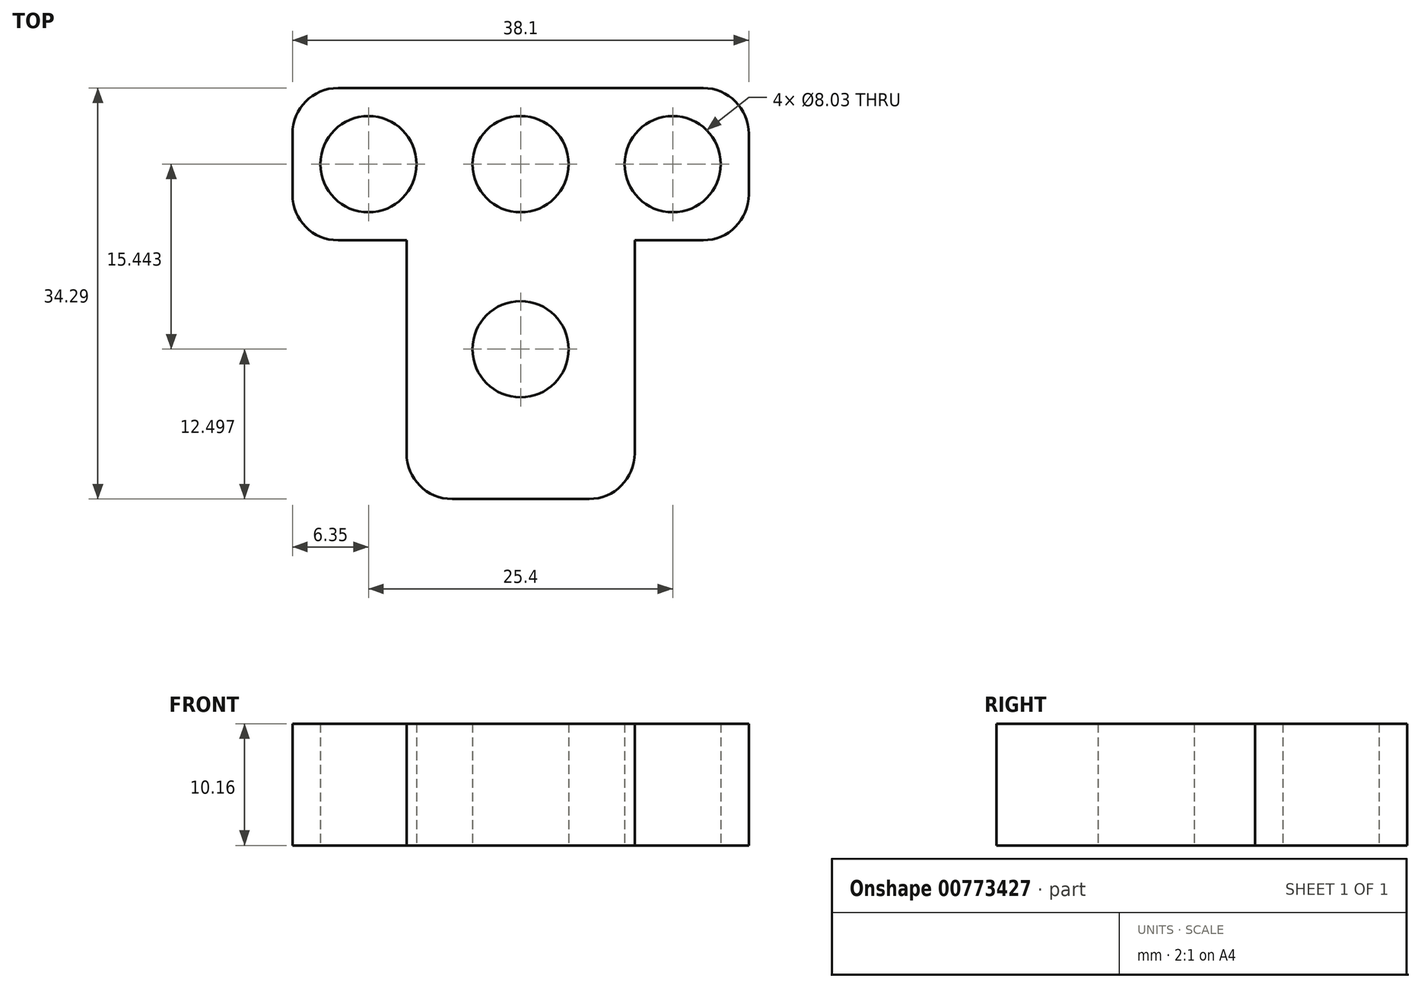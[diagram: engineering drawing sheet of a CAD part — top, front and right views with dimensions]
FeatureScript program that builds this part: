
annotation { "Feature Type Name" : "Feature", "Feature Type Description" : "" }
export const myFeature = defineFeature(function(context is Context, id is Id, definition is map)
    precondition{}
    {
        {
            var Q0;
            Q0=qCreatedBy(makeId("Top.planeOp"),FACE);
            var sketch = newSketch(context, id + "F0", { "sketchPlane" : qUnion([Q0])});
            skLineSegment(sketch, "E0.bottom", {"start": v(19.05, -6.35) * mm, "end": v(-19.05, -6.35) * mm});
            skLineSegment(sketch, "E0.top", {"start": v(19.05, 6.35) * mm, "end": v(-19.05, 6.35) * mm});
            skLineSegment(sketch, "E0.left", {"start": v(19.05, -6.35) * mm, "end": v(19.05, 6.35) * mm});
            skLineSegment(sketch, "E0.right", {"start": v(-19.05, -6.35) * mm, "end": v(-19.05, 6.35) * mm});
            skPoint(sketch, "E0.middle", {"position": v(0, 0) * mm});
            skLineSegment(sketch, "E1.bottom", {"start": v(-9.53, -6.35) * mm, "end": v(9.52, -6.35) * mm});
            skLineSegment(sketch, "E1.top", {"start": v(-9.53, -27.94) * mm, "end": v(9.53, -27.94) * mm});
            skLineSegment(sketch, "E1.left", {"start": v(-9.53, -6.35) * mm, "end": v(-9.53, -27.94) * mm});
            skLineSegment(sketch, "E1.right", {"start": v(9.52, -6.35) * mm, "end": v(9.52, -27.94) * mm});
            skCircle(sketch, "E2", {"center": v(0, 0) * mm, "radius": 4.01 * mm});
            skCircle(sketch, "E3", {"center": v(-12.7, 0) * mm, "radius": 4.01 * mm});
            skCircle(sketch, "E4", {"center": v(12.7, 0) * mm, "radius": 4.01 * mm});
            skCircle(sketch, "E5", {"center": v(0, -15.44) * mm, "radius": 4.01 * mm});
            skPoint(sketch, "E5.centerSnap0", {"position": v(0, -27.94) * mm});
            skSolve(sketch);
        }
        {
            var Q0;
            Q0=makeQuery(id+"F0.imprint","IMPRINT",FACE,{"disambiguationData":[TD([[makeQuery(id+"F0.imprint","IMPRINT",EDGE,{"derivedFrom":sQuery(id+"F0.wireOp",EDGE,"E0.top")}),1.0]])]});
            var Q1;
            Q1=makeQuery(id+"F0.imprint","IMPRINT",FACE,{"disambiguationData":[TD([[makeQuery(id+"F0.imprint","IMPRINT",EDGE,{"derivedFrom":sQuery(id+"F0.wireOp",EDGE,"E1.top")}),1.0]])]});
            extrude(context, id + "F1", {"entities" : qUnion([Q0, Q1]), "depth" : 10.16 * mm});
        }
        {
            var Q0;
            Q0=makeQuery(id+"F1.opExtrude","SWEPT_EDGE",EDGE,{"disambiguationData":[OSD([sQuery(id+"F0.wireOp",EDGE,"E1.top"),sQuery(id+"F0.wireOp",EDGE,"E1.left")])]});
            var Q1;
            Q1=makeQuery(id+"F1.opExtrude","SWEPT_EDGE",EDGE,{"disambiguationData":[OSD([sQuery(id+"F0.wireOp",EDGE,"E1.top"),sQuery(id+"F0.wireOp",EDGE,"E1.right")])]});
            var Q2;
            Q2=makeQuery(id+"F1.opExtrude","SWEPT_EDGE",EDGE,{"disambiguationData":[OSD([sQuery(id+"F0.wireOp",EDGE,"E0.bottom"),sQuery(id+"F0.wireOp",EDGE,"E0.left")])]});
            var Q3;
            Q3=makeQuery(id+"F1.opExtrude","SWEPT_EDGE",EDGE,{"disambiguationData":[OSD([sQuery(id+"F0.wireOp",EDGE,"E0.top"),sQuery(id+"F0.wireOp",EDGE,"E0.left")])]});
            var Q4;
            Q4=makeQuery(id+"F1.opExtrude","SWEPT_EDGE",EDGE,{"disambiguationData":[OSD([sQuery(id+"F0.wireOp",EDGE,"E0.bottom"),sQuery(id+"F0.wireOp",EDGE,"E0.right")])]});
            var Q5;
            Q5=makeQuery(id+"F1.opExtrude","SWEPT_EDGE",EDGE,{"disambiguationData":[OSD([sQuery(id+"F0.wireOp",EDGE,"E0.top"),sQuery(id+"F0.wireOp",EDGE,"E0.right")])]});
            fillet(context, id + "F2", {"entities" : qUnion([Q0, Q1, Q2, Q3, Q4, Q5]), "radius" : 3.8 * mm, "tangentPropagation" : true, "allowEdgeOverflow" : false});
        }
    });
